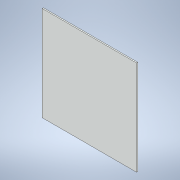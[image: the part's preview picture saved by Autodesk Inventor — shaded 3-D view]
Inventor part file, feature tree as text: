
AUTODESK INVENTOR PART (.ipt)
format: ipt  version: 2021 (Build 250183000, 183)  size: 90,112 bytes
history: native  units: in
note: dims shown in document units (in); Inventor stores cm internally (conversion verified against a paired STEP export)
features: extrude x1, sketch x1
ambient origin geometry x8: Origin, YZ Plane, XZ Plane, XY Plane, X Axis, Y Axis, Z Axis, Center Point
bodies: Solid1 (feature_tree)
feature tree (2):
  extrude  "Extrusion1"  Depth=3.0in
  sketch  "Sketch1"  dims[d0=3.0in d1=3.0in d2=0.0394in d3=0.0in]
